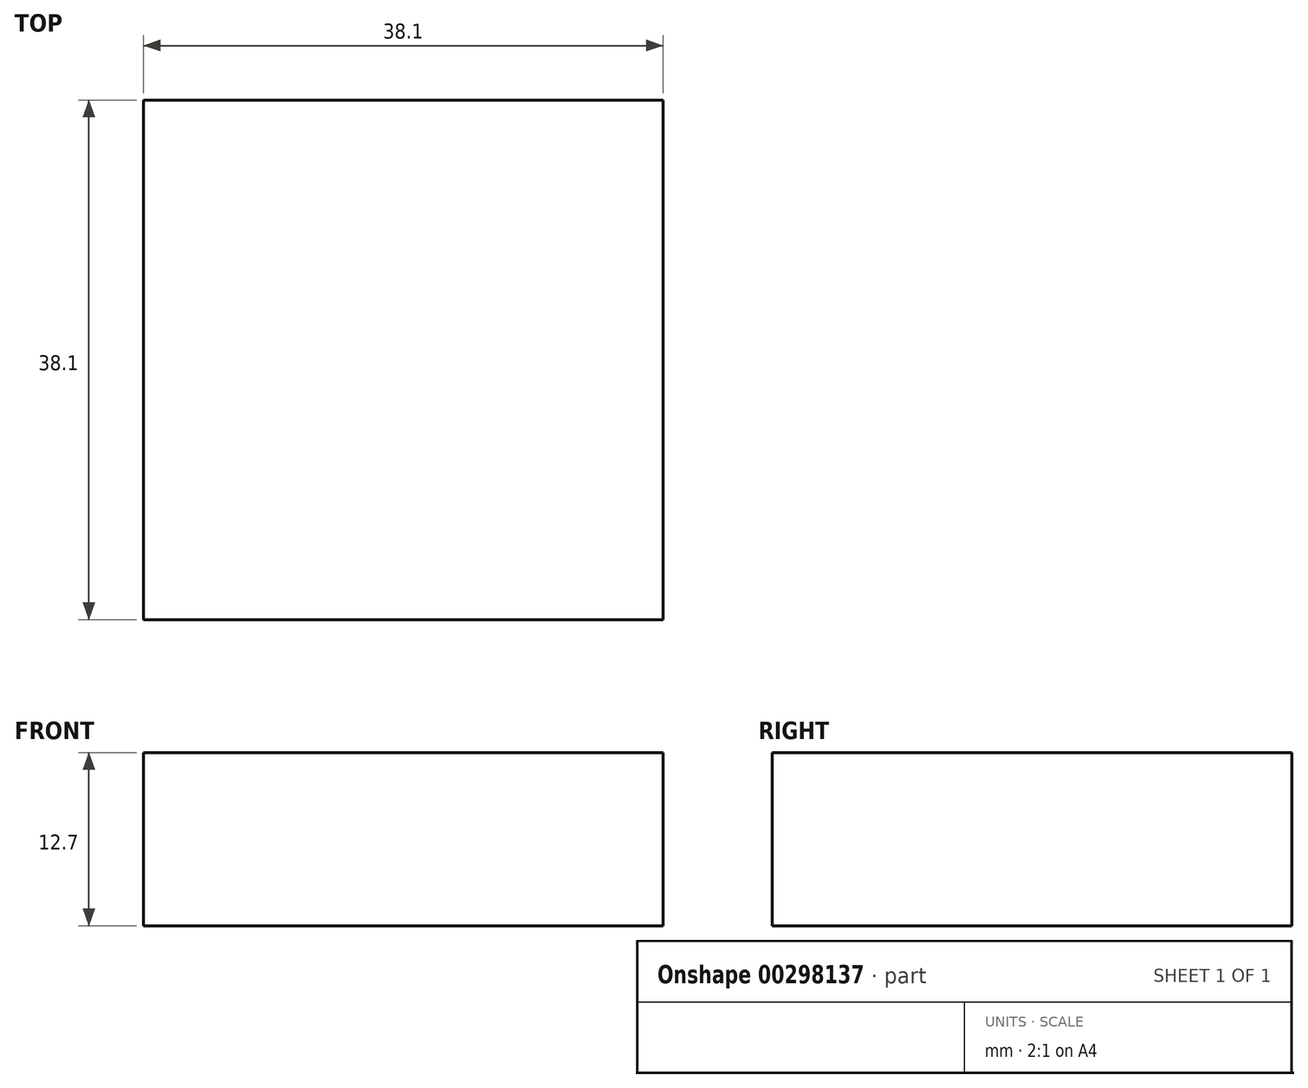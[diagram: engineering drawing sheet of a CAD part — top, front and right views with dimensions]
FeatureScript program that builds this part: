
annotation { "Feature Type Name" : "Feature", "Feature Type Description" : "" }
export const myFeature = defineFeature(function(context is Context, id is Id, definition is map)
    precondition{}
    {
        {
            var Q0;
            Q0=qCreatedBy(makeId("Top.planeOp"),FACE);
            var sketch = newSketch(context, id + "F0", { "sketchPlane" : qUnion([Q0])});
            skLineSegment(sketch, "E0.bottom", {"start": v(0, 0) * mm, "end": v(38.1, 0) * mm});
            skLineSegment(sketch, "E0.top", {"start": v(0, -38.1) * mm, "end": v(38.1, -38.1) * mm});
            skLineSegment(sketch, "E0.left", {"start": v(0, 0) * mm, "end": v(0, -38.1) * mm});
            skLineSegment(sketch, "E0.right", {"start": v(38.1, 0) * mm, "end": v(38.1, -38.1) * mm});
            skSolve(sketch);
        }
        {
            var Q0;
            Q0 = qSketchRegion(id + "F0", true);
            extrude(context, id + "F1", {"entities" : qUnion([Q0]), "depth" : 12.7 * mm});
        }
    });
